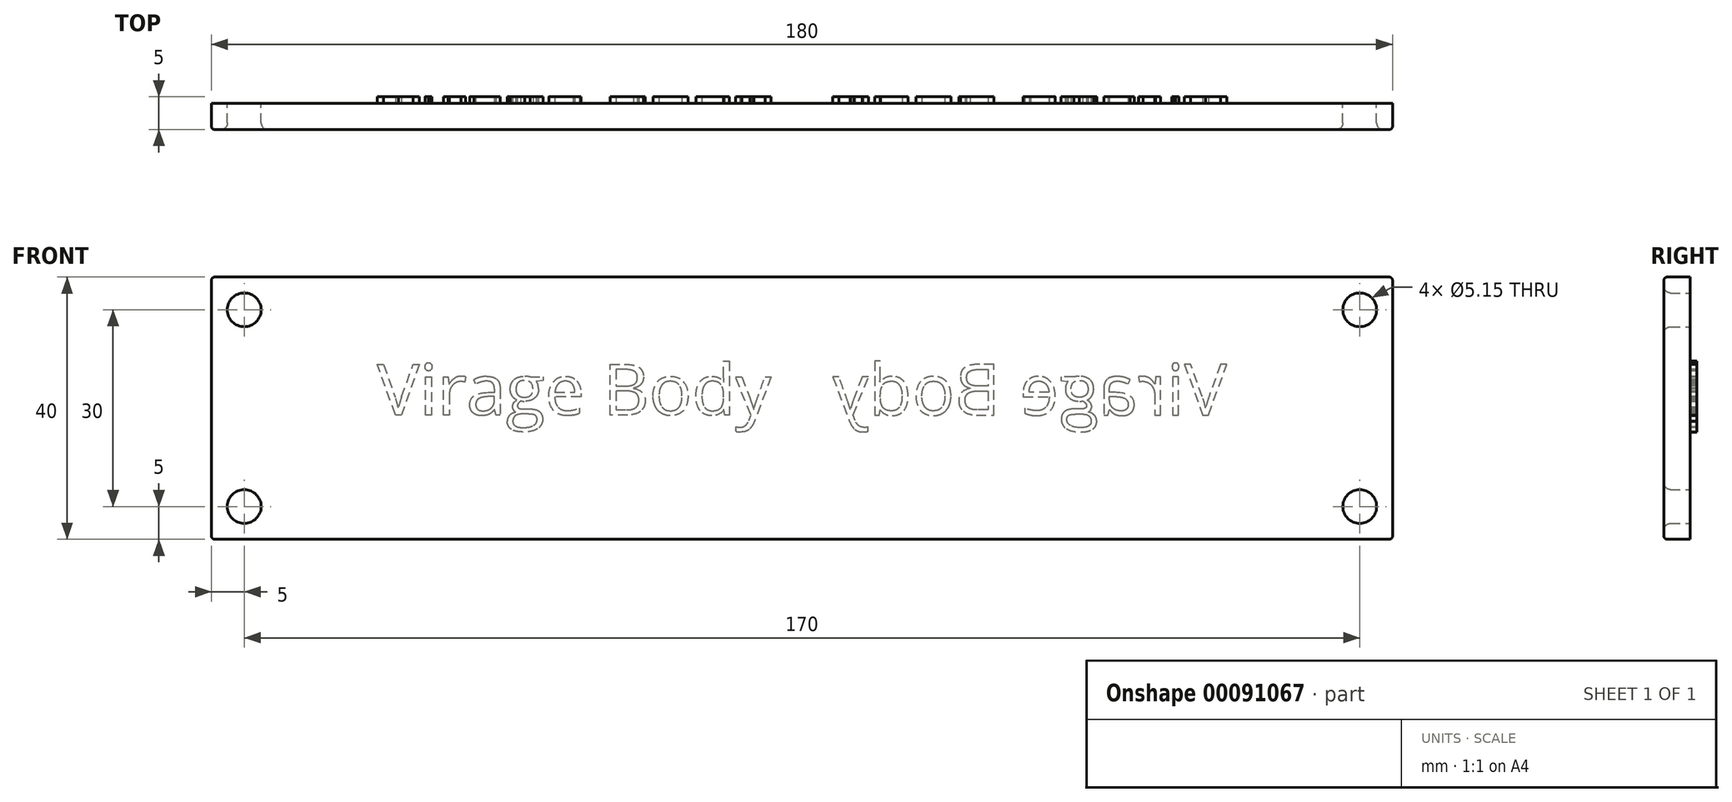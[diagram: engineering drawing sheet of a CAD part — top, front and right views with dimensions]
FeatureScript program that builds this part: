
annotation { "Feature Type Name" : "Feature", "Feature Type Description" : "" }
export const myFeature = defineFeature(function(context is Context, id is Id, definition is map)
    precondition{}
    {
        {
            var Q0;
            Q0=qCreatedBy(makeId("Front.planeOp"),FACE);
            var sketch = newSketch(context, id + "F0", { "sketchPlane" : qUnion([Q0])});
            skLineSegment(sketch, "E0.bottom", {"start": v(-90, -20) * mm, "end": v(90, -20) * mm});
            skLineSegment(sketch, "E0.top", {"start": v(-90, 20) * mm, "end": v(90, 20) * mm});
            skLineSegment(sketch, "E0.left", {"start": v(-90, -20) * mm, "end": v(-90, 20) * mm});
            skLineSegment(sketch, "E0.right", {"start": v(90, -20) * mm, "end": v(90, 20) * mm});
            skPoint(sketch, "E0.middle", {"position": v(0, 0) * mm});
            skCircle(sketch, "E1", {"center": v(-85, 15) * mm, "radius": 2.58 * mm});
            skPoint(sketch, "E2.start.orphan", {"position": v(-90, 0) * mm});
            skPoint(sketch, "E3.orphan", {"position": v(0, 20) * mm});
            skPoint(sketch, "E4.end.orphan", {"position": v(0, -20) * mm});
            skLineSegment(sketch, "E5", {"start": v(-90, 0) * mm, "end": v(0, 0) * mm, "construction": true});
            skLineSegment(sketch, "E6", {"start": v(0, 20) * mm, "end": v(0, -20) * mm, "construction": true});
            skCircle(sketch, "E7.MirrorC", {"center": v(-85, -15) * mm, "radius": 2.58 * mm});
            skCircle(sketch, "E8.MirrorC", {"center": v(85, 15) * mm, "radius": 2.58 * mm});
            skCircle(sketch, "E9.MirrorC", {"center": v(85, -15) * mm, "radius": 2.58 * mm});
            skSolve(sketch);
        }
        {
            var Q0;
            Q0=makeQuery(id+"F0.imprint","IMPRINT",FACE,{"disambiguationData":[TD([[makeQuery(id+"F0.imprint","IMPRINT",EDGE,{"derivedFrom":sQuery(id+"F0.wireOp",EDGE,"E0.bottom")}),1.0]])]});
            extrude(context, id + "F1", {"entities" : qUnion([Q0]), "depth" : 4 * mm});
        }
        {
            var Q0;
            Q0=makeQuery(id+"F1.opExtrude","CAP_EDGE",EDGE,{"disambiguationData":[OSD([sQuery(id+"F0.wireOp",EDGE,"E1")])],"isStart":false});
            var Q1;
            Q1=makeQuery(id+"F1.opExtrude","CAP_EDGE",EDGE,{"disambiguationData":[OSD([sQuery(id+"F0.wireOp",EDGE,"f5b72a5b-8583-449a-bdbf-9ac5a681e1fd0.MirrorC")])],"isStart":false});
            var Q2;
            Q2=makeQuery(id+"F1.opExtrude","CAP_EDGE",EDGE,{"disambiguationData":[OSD([sQuery(id+"F0.wireOp",EDGE,"2623e306-60f4-4522-aa65-1e3e8c2cf5b60.MirrorC")])],"isStart":false});
            var Q3;
            Q3=makeQuery(id+"F1.opExtrude","CAP_EDGE",EDGE,{"disambiguationData":[OSD([sQuery(id+"F0.wireOp",EDGE,"be81a34d-1d50-4ce7-a7a8-4484a1701fac0.MirrorC")])],"isStart":false});
            var Q4;
            Q4=makeQuery(id+"F1.opExtrude","CAP_EDGE",EDGE,{"disambiguationData":[OSD([sQuery(id+"F0.wireOp",EDGE,"E7.MirrorC")])],"isStart":false});
            var Q5;
            Q5=makeQuery(id+"F1.opExtrude","CAP_EDGE",EDGE,{"disambiguationData":[OSD([sQuery(id+"F0.wireOp",EDGE,"E8.MirrorC")])],"isStart":false});
            var Q6;
            Q6=makeQuery(id+"F1.opExtrude","CAP_EDGE",EDGE,{"disambiguationData":[OSD([sQuery(id+"F0.wireOp",EDGE,"E9.MirrorC")])],"isStart":false});
            fillet(context, id + "F2", {"entities" : qUnion([Q0, Q1, Q2, Q3, Q4, Q5, Q6]), "radius" : 1 * mm, "tangentPropagation" : true, "allowEdgeOverflow" : false});
        }
        {
            var Q0;
            Q0=makeQuery(id+"F1.opExtrude","CAP_EDGE",EDGE,{"disambiguationData":[OSD([sQuery(id+"F0.wireOp",EDGE,"E0.top")])],"isStart":false});
            var Q1;
            Q1=makeQuery(id+"F1.opExtrude","CAP_EDGE",EDGE,{"disambiguationData":[OSD([sQuery(id+"F0.wireOp",EDGE,"E0.left")])],"isStart":false});
            var Q2;
            Q2=makeQuery(id+"F1.opExtrude","CAP_EDGE",EDGE,{"disambiguationData":[OSD([sQuery(id+"F0.wireOp",EDGE,"E0.bottom")])],"isStart":false});
            var Q3;
            Q3=makeQuery(id+"F1.opExtrude","CAP_EDGE",EDGE,{"disambiguationData":[OSD([sQuery(id+"F0.wireOp",EDGE,"E0.right")])],"isStart":false});
            var Q4;
            Q4=makeQuery(id+"F1.opExtrude","SWEPT_EDGE",EDGE,{"disambiguationData":[OSD([sQuery(id+"F0.wireOp",EDGE,"E0.top"),sQuery(id+"F0.wireOp",EDGE,"E0.left")])]});
            var Q5;
            Q5=makeQuery(id+"F1.opExtrude","SWEPT_EDGE",EDGE,{"disambiguationData":[OSD([sQuery(id+"F0.wireOp",EDGE,"E0.bottom"),sQuery(id+"F0.wireOp",EDGE,"E0.left")])]});
            var Q6;
            Q6=makeQuery(id+"F1.opExtrude","SWEPT_EDGE",EDGE,{"disambiguationData":[OSD([sQuery(id+"F0.wireOp",EDGE,"E0.top"),sQuery(id+"F0.wireOp",EDGE,"E0.right")])]});
            var Q7;
            Q7=makeQuery(id+"F1.opExtrude","SWEPT_EDGE",EDGE,{"disambiguationData":[OSD([sQuery(id+"F0.wireOp",EDGE,"E0.bottom"),sQuery(id+"F0.wireOp",EDGE,"E0.right")])]});
            fillet(context, id + "F3", {"entities" : qUnion([Q0, Q1, Q2, Q3, Q4, Q5, Q6, Q7]), "radius" : .5 * mm, "tangentPropagation" : true, "allowEdgeOverflow" : false});
        }
        {
            var Q0;
            Q0=makeQuery(id+"F1.opExtrude","CAP_FACE",FACE,{"disambiguationData":[OSD([sQuery(id+"F0.wireOp",EDGE,"E0.bottom"),sQuery(id+"F0.wireOp",EDGE,"E0.top"),sQuery(id+"F0.wireOp",EDGE,"E0.left"),sQuery(id+"F0.wireOp",EDGE,"E0.right"),sQuery(id+"F0.wireOp",EDGE,"E1"),sQuery(id+"F0.wireOp",EDGE,"E7.MirrorC"),sQuery(id+"F0.wireOp",EDGE,"E8.MirrorC"),sQuery(id+"F0.wireOp",EDGE,"E9.MirrorC")])],"isStart":true});
            var sketch = newSketch(context, id + "F4", { "sketchPlane" : qUnion([Q0])});
            skText(sketch, "E10", { "text": "Virage Body", "fontName": "OpenSans-Regular.ttf"});
            skLineSegment(sketch, "E11", {"start": v(0, 20) * mm, "end": v(0, -20) * mm, "construction": true});
            const initialGuessF4  = {"E10": [-0.06473, -0.00103, 1, 0, 0.00779]};
            skSetInitialGuess(sketch, initialGuessF4);
            skSolve(sketch);
        }
        {
            var Q0;
            Q0=qSketchRegion(id+"F4",true);
            extrude(context, id + "F5", {"entities" : qUnion([Q0]), "operationType" : NewBodyOperationType.ADD, "depth" : 1 * mm});
        }
        {
            var Q0;
            Q0=makeQuery(id+"F1.opExtrude","SWEPT_BODY",BODY,{"disambiguationData":[OSD([sQuery(id+"F0.wireOp",EDGE,"E0.bottom"),sQuery(id+"F0.wireOp",EDGE,"E0.top"),sQuery(id+"F0.wireOp",EDGE,"E0.left"),sQuery(id+"F0.wireOp",EDGE,"E0.right"),sQuery(id+"F0.wireOp",EDGE,"E1"),sQuery(id+"F0.wireOp",EDGE,"E7.MirrorC"),sQuery(id+"F0.wireOp",EDGE,"E8.MirrorC"),sQuery(id+"F0.wireOp",EDGE,"E9.MirrorC")])]});
            var Q1;
            Q1=makeQuery(id+"F5.opExtrude","SWEPT_FACE",FACE,{"disambiguationData":[OSD([sQuery(id+"F4.wireOp",EDGE,"E10.sketch_text.stroke-94")])]});
            var Q2;
            Q2=makeQuery(id+"F5.opExtrude","SWEPT_FACE",FACE,{"disambiguationData":[OSD([sQuery(id+"F4.wireOp",EDGE,"E10.sketch_text.stroke-169")])]});
            var Q3;
            Q3=makeQuery(id+"F5.opExtrude","SWEPT_FACE",FACE,{"disambiguationData":[OSD([sQuery(id+"F4.wireOp",EDGE,"E10.sketch_text.stroke-185")])]});
            var Q4;
            Q4=makeQuery(id+"F5.opExtrude","SWEPT_FACE",FACE,{"disambiguationData":[OSD([sQuery(id+"F4.wireOp",EDGE,"E10.sketch_text.stroke-125")])]});
            var Q5;
            Q5=makeQuery(id+"F5.opExtrude","SWEPT_FACE",FACE,{"disambiguationData":[OSD([sQuery(id+"F4.wireOp",EDGE,"E10.sketch_text.stroke-155")])]});
            var Q6;
            Q6=makeQuery(id+"F5.opExtrude","SWEPT_FACE",FACE,{"disambiguationData":[OSD([sQuery(id+"F4.wireOp",EDGE,"E10.sketch_text.stroke-65")])]});
            var Q7;
            Q7=makeQuery(id+"F5.opExtrude","SWEPT_FACE",FACE,{"disambiguationData":[OSD([sQuery(id+"F4.wireOp",EDGE,"E10.sketch_text.stroke-81")])]});
            var Q8;
            Q8=makeQuery(id+"F5.opExtrude","SWEPT_FACE",FACE,{"disambiguationData":[OSD([sQuery(id+"F4.wireOp",EDGE,"E10.sketch_text.stroke-67")])]});
            var Q9;
            Q9=makeQuery(id+"F5.opExtrude","SWEPT_FACE",FACE,{"disambiguationData":[OSD([sQuery(id+"F4.wireOp",EDGE,"E10.sketch_text.stroke-99")])]});
            var Q10;
            Q10=makeQuery(id+"F5.opExtrude","SWEPT_FACE",FACE,{"disambiguationData":[OSD([sQuery(id+"F4.wireOp",EDGE,"E10.sketch_text.stroke-127")])]});
            var Q11;
            Q11=makeQuery(id+"F5.opExtrude","SWEPT_FACE",FACE,{"disambiguationData":[OSD([sQuery(id+"F4.wireOp",EDGE,"E10.sketch_text.stroke-10")])]});
            var Q12;
            Q12=makeQuery(id+"F5.opExtrude","CAP_FACE",FACE,{"disambiguationData":[OSD([sQuery(id+"F4.wireOp",EDGE,"E10.sketch_text.stroke-9"),sQuery(id+"F4.wireOp",EDGE,"E10.sketch_text.stroke-10"),sQuery(id+"F4.wireOp",EDGE,"E10.sketch_text.stroke-11"),sQuery(id+"F4.wireOp",EDGE,"E10.sketch_text.stroke-12")])],"isStart":false});
            var Q13;
            Q13=makeQuery(id+"F5.opExtrude","SWEPT_FACE",FACE,{"disambiguationData":[OSD([sQuery(id+"F4.wireOp",EDGE,"E10.sketch_text.stroke-154")])]});
            var Q14;
            Q14=makeQuery(id+"F5.opExtrude","SWEPT_FACE",FACE,{"disambiguationData":[OSD([sQuery(id+"F4.wireOp",EDGE,"E10.sketch_text.stroke-1")])]});
            var Q15;
            Q15=makeQuery(id+"F5.opExtrude","CAP_FACE",FACE,{"disambiguationData":[OSD([sQuery(id+"F4.wireOp",EDGE,"E10.sketch_text.stroke-124"),sQuery(id+"F4.wireOp",EDGE,"E10.sketch_text.stroke-125"),sQuery(id+"F4.wireOp",EDGE,"E10.sketch_text.stroke-126"),sQuery(id+"F4.wireOp",EDGE,"E10.sketch_text.stroke-127"),sQuery(id+"F4.wireOp",EDGE,"E10.sketch_text.stroke-128"),sQuery(id+"F4.wireOp",EDGE,"E10.sketch_text.stroke-129"),sQuery(id+"F4.wireOp",EDGE,"E10.sketch_text.stroke-130"),sQuery(id+"F4.wireOp",EDGE,"E10.sketch_text.stroke-131"),sQuery(id+"F4.wireOp",EDGE,"E10.sketch_text.stroke-132"),sQuery(id+"F4.wireOp",EDGE,"E10.sketch_text.stroke-133"),sQuery(id+"F4.wireOp",EDGE,"E10.sketch_text.stroke-134"),sQuery(id+"F4.wireOp",EDGE,"E10.sketch_text.stroke-135"),sQuery(id+"F4.wireOp",EDGE,"E10.sketch_text.stroke-136"),sQuery(id+"F4.wireOp",EDGE,"E10.sketch_text.stroke-137"),sQuery(id+"F4.wireOp",EDGE,"E10.sketch_text.stroke-138")])],"isStart":false});
            var Q16;
            Q16=makeQuery(id+"F5.opExtrude","CAP_FACE",FACE,{"disambiguationData":[OSD([sQuery(id+"F4.wireOp",EDGE,"E10.sketch_text.stroke-34"),sQuery(id+"F4.wireOp",EDGE,"E10.sketch_text.stroke-35"),sQuery(id+"F4.wireOp",EDGE,"E10.sketch_text.stroke-36"),sQuery(id+"F4.wireOp",EDGE,"E10.sketch_text.stroke-37"),sQuery(id+"F4.wireOp",EDGE,"E10.sketch_text.stroke-38"),sQuery(id+"F4.wireOp",EDGE,"E10.sketch_text.stroke-39"),sQuery(id+"F4.wireOp",EDGE,"E10.sketch_text.stroke-40"),sQuery(id+"F4.wireOp",EDGE,"E10.sketch_text.stroke-41"),sQuery(id+"F4.wireOp",EDGE,"E10.sketch_text.stroke-42"),sQuery(id+"F4.wireOp",EDGE,"E10.sketch_text.stroke-43"),sQuery(id+"F4.wireOp",EDGE,"E10.sketch_text.stroke-44"),sQuery(id+"F4.wireOp",EDGE,"E10.sketch_text.stroke-45"),sQuery(id+"F4.wireOp",EDGE,"E10.sketch_text.stroke-46"),sQuery(id+"F4.wireOp",EDGE,"E10.sketch_text.stroke-47"),sQuery(id+"F4.wireOp",EDGE,"E10.sketch_text.stroke-48"),sQuery(id+"F4.wireOp",EDGE,"E10.sketch_text.stroke-49"),sQuery(id+"F4.wireOp",EDGE,"E10.sketch_text.stroke-50"),sQuery(id+"F4.wireOp",EDGE,"E10.sketch_text.stroke-51"),sQuery(id+"F4.wireOp",EDGE,"E10.sketch_text.stroke-52"),sQuery(id+"F4.wireOp",EDGE,"E10.sketch_text.stroke-53"),sQuery(id+"F4.wireOp",EDGE,"E10.sketch_text.stroke-54"),sQuery(id+"F4.wireOp",EDGE,"E10.sketch_text.stroke-55"),sQuery(id+"F4.wireOp",EDGE,"E10.sketch_text.stroke-56"),sQuery(id+"F4.wireOp",EDGE,"E10.sketch_text.stroke-57"),sQuery(id+"F4.wireOp",EDGE,"E10.sketch_text.stroke-58"),sQuery(id+"F4.wireOp",EDGE,"E10.sketch_text.stroke-59"),sQuery(id+"F4.wireOp",EDGE,"E10.sketch_text.stroke-60")])],"isStart":false});
            var Q17;
            Q17=makeQuery(id+"F5.opExtrude","SWEPT_FACE",FACE,{"disambiguationData":[OSD([sQuery(id+"F4.wireOp",EDGE,"E10.sketch_text.stroke-50")])]});
            var Q18;
            Q18=makeQuery(id+"F5.opExtrude","SWEPT_FACE",FACE,{"disambiguationData":[OSD([sQuery(id+"F4.wireOp",EDGE,"E10.sketch_text.stroke-2")])]});
            var Q19;
            Q19=makeQuery(id+"F5.opExtrude","SWEPT_FACE",FACE,{"disambiguationData":[OSD([sQuery(id+"F4.wireOp",EDGE,"E10.sketch_text.stroke-3")])]});
            var Q20;
            Q20=makeQuery(id+"F5.opExtrude","SWEPT_FACE",FACE,{"disambiguationData":[OSD([sQuery(id+"F4.wireOp",EDGE,"E10.sketch_text.stroke-5")])]});
            var Q21;
            Q21=makeQuery(id+"F5.opExtrude","SWEPT_FACE",FACE,{"disambiguationData":[OSD([sQuery(id+"F4.wireOp",EDGE,"E10.sketch_text.stroke-8")])]});
            var Q22;
            Q22=makeQuery(id+"F5.opExtrude","SWEPT_FACE",FACE,{"disambiguationData":[OSD([sQuery(id+"F4.wireOp",EDGE,"E10.sketch_text.stroke-98")])]});
            var Q23;
            Q23=makeQuery(id+"F5.opExtrude","SWEPT_FACE",FACE,{"disambiguationData":[OSD([sQuery(id+"F4.wireOp",EDGE,"E10.sketch_text.stroke-66")])]});
            var Q24;
            Q24=makeQuery(id+"F5.opExtrude","SWEPT_FACE",FACE,{"disambiguationData":[OSD([sQuery(id+"F4.wireOp",EDGE,"E10.sketch_text.stroke-153")])]});
            var Q25;
            Q25=makeQuery(id+"F5.opExtrude","SWEPT_FACE",FACE,{"disambiguationData":[OSD([sQuery(id+"F4.wireOp",EDGE,"E10.sketch_text.stroke-126")])]});
            var Q26;
            Q26=makeQuery(id+"F5.opExtrude","SWEPT_FACE",FACE,{"disambiguationData":[OSD([sQuery(id+"F4.wireOp",EDGE,"E10.sketch_text.stroke-183")])]});
            var Q27;
            Q27=makeQuery(id+"F5.opExtrude","SWEPT_FACE",FACE,{"disambiguationData":[OSD([sQuery(id+"F4.wireOp",EDGE,"E10.sketch_text.stroke-109")])]});
            var Q28;
            Q28=makeQuery(id+"F5.opExtrude","SWEPT_FACE",FACE,{"disambiguationData":[OSD([sQuery(id+"F4.wireOp",EDGE,"E10.sketch_text.stroke-186")])]});
            var Q29;
            Q29=makeQuery(id+"F5.opExtrude","SWEPT_FACE",FACE,{"disambiguationData":[OSD([sQuery(id+"F4.wireOp",EDGE,"E10.sketch_text.stroke-79")])]});
            var Q30;
            Q30=makeQuery(id+"F5.opExtrude","SWEPT_FACE",FACE,{"disambiguationData":[OSD([sQuery(id+"F4.wireOp",EDGE,"E10.sketch_text.stroke-110")])]});
            var Q31;
            Q31=makeQuery(id+"F5.opExtrude","SWEPT_FACE",FACE,{"disambiguationData":[OSD([sQuery(id+"F4.wireOp",EDGE,"E10.sketch_text.stroke-38")])]});
            var Q32;
            Q32=makeQuery(id+"F5.opExtrude","SWEPT_FACE",FACE,{"disambiguationData":[OSD([sQuery(id+"F4.wireOp",EDGE,"E10.sketch_text.stroke-24")])]});
            var Q33;
            Q33=makeQuery(id+"F5.opExtrude","SWEPT_FACE",FACE,{"disambiguationData":[OSD([sQuery(id+"F4.wireOp",EDGE,"E10.sketch_text.stroke-12")])]});
            var Q34;
            Q34=makeQuery(id+"F5.opExtrude","SWEPT_FACE",FACE,{"disambiguationData":[OSD([sQuery(id+"F4.wireOp",EDGE,"E10.sketch_text.stroke-100")])]});
            var Q35;
            Q35=makeQuery(id+"F5.opExtrude","SWEPT_FACE",FACE,{"disambiguationData":[OSD([sQuery(id+"F4.wireOp",EDGE,"E10.sketch_text.stroke-158")])]});
            var Q36;
            Q36=makeQuery(id+"F5.opExtrude","SWEPT_FACE",FACE,{"disambiguationData":[OSD([sQuery(id+"F4.wireOp",EDGE,"E10.sketch_text.stroke-142")])]});
            var Q37;
            Q37=makeQuery(id+"F5.opExtrude","SWEPT_FACE",FACE,{"disambiguationData":[OSD([sQuery(id+"F4.wireOp",EDGE,"E10.sketch_text.stroke-54")])]});
            var Q38;
            Q38=makeQuery(id+"F5.opExtrude","SWEPT_FACE",FACE,{"disambiguationData":[OSD([sQuery(id+"F4.wireOp",EDGE,"E10.sketch_text.stroke-25")])]});
            var Q39;
            Q39=makeQuery(id+"F5.opExtrude","SWEPT_FACE",FACE,{"disambiguationData":[OSD([sQuery(id+"F4.wireOp",EDGE,"E10.sketch_text.stroke-101")])]});
            var Q40;
            Q40=makeQuery(id+"F5.opExtrude","SWEPT_FACE",FACE,{"disambiguationData":[OSD([sQuery(id+"F4.wireOp",EDGE,"E10.sketch_text.stroke-69")])]});
            var Q41;
            Q41=makeQuery(id+"F5.opExtrude","SWEPT_FACE",FACE,{"disambiguationData":[OSD([sQuery(id+"F4.wireOp",EDGE,"E10.sketch_text.stroke-159")])]});
            var Q42;
            Q42=makeQuery(id+"F5.opExtrude","SWEPT_FACE",FACE,{"disambiguationData":[OSD([sQuery(id+"F4.wireOp",EDGE,"E10.sketch_text.stroke-85")])]});
            var Q43;
            Q43=makeQuery(id+"F5.opExtrude","SWEPT_FACE",FACE,{"disambiguationData":[OSD([sQuery(id+"F4.wireOp",EDGE,"E10.sketch_text.stroke-173")])]});
            var Q44;
            Q44=makeQuery(id+"F5.opExtrude","SWEPT_FACE",FACE,{"disambiguationData":[OSD([sQuery(id+"F4.wireOp",EDGE,"E10.sketch_text.stroke-40")])]});
            var Q45;
            Q45=makeQuery(id+"F5.opExtrude","SWEPT_FACE",FACE,{"disambiguationData":[OSD([sQuery(id+"F4.wireOp",EDGE,"E10.sketch_text.stroke-102")])]});
            var Q46;
            Q46=makeQuery(id+"F5.opExtrude","SWEPT_FACE",FACE,{"disambiguationData":[OSD([sQuery(id+"F4.wireOp",EDGE,"E10.sketch_text.stroke-86")])]});
            var Q47;
            Q47=makeQuery(id+"F5.opExtrude","SWEPT_FACE",FACE,{"disambiguationData":[OSD([sQuery(id+"F4.wireOp",EDGE,"E10.sketch_text.stroke-130")])]});
            var Q48;
            Q48=makeQuery(id+"F5.opExtrude","SWEPT_FACE",FACE,{"disambiguationData":[OSD([sQuery(id+"F4.wireOp",EDGE,"E10.sketch_text.stroke-103")])]});
            var Q49;
            Q49=makeQuery(id+"F5.opExtrude","SWEPT_FACE",FACE,{"disambiguationData":[OSD([sQuery(id+"F4.wireOp",EDGE,"E10.sketch_text.stroke-87")])]});
            var Q50;
            Q50=makeQuery(id+"F5.opExtrude","SWEPT_FACE",FACE,{"disambiguationData":[OSD([sQuery(id+"F4.wireOp",EDGE,"E10.sketch_text.stroke-145")])]});
            var Q51;
            Q51=makeQuery(id+"F5.opExtrude","SWEPT_FACE",FACE,{"disambiguationData":[OSD([sQuery(id+"F4.wireOp",EDGE,"E10.sketch_text.stroke-131")])]});
            var Q52;
            Q52=makeQuery(id+"F5.opExtrude","SWEPT_FACE",FACE,{"disambiguationData":[OSD([sQuery(id+"F4.wireOp",EDGE,"E10.sketch_text.stroke-28")])]});
            var Q53;
            Q53=makeQuery(id+"F5.opExtrude","SWEPT_FACE",FACE,{"disambiguationData":[OSD([sQuery(id+"F4.wireOp",EDGE,"E10.sketch_text.stroke-14")])]});
            var Q54;
            Q54=makeQuery(id+"F5.opExtrude","SWEPT_FACE",FACE,{"disambiguationData":[OSD([sQuery(id+"F4.wireOp",EDGE,"E10.sketch_text.stroke-88")])]});
            var Q55;
            Q55=makeQuery(id+"F5.opExtrude","SWEPT_FACE",FACE,{"disambiguationData":[OSD([sQuery(id+"F4.wireOp",EDGE,"E10.sketch_text.stroke-162")])]});
            var Q56;
            Q56=makeQuery(id+"F5.opExtrude","SWEPT_FACE",FACE,{"disambiguationData":[OSD([sQuery(id+"F4.wireOp",EDGE,"E10.sketch_text.stroke-176")])]});
            var Q57;
            Q57=makeQuery(id+"F5.opExtrude","SWEPT_FACE",FACE,{"disambiguationData":[OSD([sQuery(id+"F4.wireOp",EDGE,"E10.sketch_text.stroke-73")])]});
            var Q58;
            Q58=makeQuery(id+"F5.opExtrude","SWEPT_FACE",FACE,{"disambiguationData":[OSD([sQuery(id+"F4.wireOp",EDGE,"E10.sketch_text.stroke-59")])]});
            var Q59;
            Q59=makeQuery(id+"F5.opExtrude","SWEPT_FACE",FACE,{"disambiguationData":[OSD([sQuery(id+"F4.wireOp",EDGE,"E10.sketch_text.stroke-133")])]});
            var Q60;
            Q60=makeQuery(id+"F5.opExtrude","SWEPT_FACE",FACE,{"disambiguationData":[OSD([sQuery(id+"F4.wireOp",EDGE,"E10.sketch_text.stroke-119")])]});
            var Q61;
            Q61=makeQuery(id+"F5.opExtrude","SWEPT_FACE",FACE,{"disambiguationData":[OSD([sQuery(id+"F4.wireOp",EDGE,"E10.sketch_text.stroke-74")])]});
            var Q62;
            Q62=makeQuery(id+"F5.opExtrude","SWEPT_FACE",FACE,{"disambiguationData":[OSD([sQuery(id+"F4.wireOp",EDGE,"E10.sketch_text.stroke-44")])]});
            var Q63;
            Q63=makeQuery(id+"F5.opExtrude","SWEPT_FACE",FACE,{"disambiguationData":[OSD([sQuery(id+"F4.wireOp",EDGE,"E10.sketch_text.stroke-120")])]});
            var Q64;
            Q64=makeQuery(id+"F5.opExtrude","SWEPT_FACE",FACE,{"disambiguationData":[OSD([sQuery(id+"F4.wireOp",EDGE,"E10.sketch_text.stroke-90")])]});
            var Q65;
            Q65=makeQuery(id+"F5.opExtrude","SWEPT_FACE",FACE,{"disambiguationData":[OSD([sQuery(id+"F4.wireOp",EDGE,"E10.sketch_text.stroke-178")])]});
            var Q66;
            Q66=makeQuery(id+"F5.opExtrude","SWEPT_FACE",FACE,{"disambiguationData":[OSD([sQuery(id+"F4.wireOp",EDGE,"E10.sketch_text.stroke-45")])]});
            var Q67;
            Q67=makeQuery(id+"F5.opExtrude","SWEPT_FACE",FACE,{"disambiguationData":[OSD([sQuery(id+"F4.wireOp",EDGE,"E10.sketch_text.stroke-31")])]});
            var Q68;
            Q68=makeQuery(id+"F5.opExtrude","SWEPT_FACE",FACE,{"disambiguationData":[OSD([sQuery(id+"F4.wireOp",EDGE,"E10.sketch_text.stroke-135")])]});
            var Q69;
            Q69=makeQuery(id+"F5.opExtrude","SWEPT_FACE",FACE,{"disambiguationData":[OSD([sQuery(id+"F4.wireOp",EDGE,"E10.sketch_text.stroke-179")])]});
            var Q70;
            Q70=makeQuery(id+"F5.opExtrude","SWEPT_FACE",FACE,{"disambiguationData":[OSD([sQuery(id+"F4.wireOp",EDGE,"E10.sketch_text.stroke-165")])]});
            var Q71;
            Q71=makeQuery(id+"F5.opExtrude","SWEPT_FACE",FACE,{"disambiguationData":[OSD([sQuery(id+"F4.wireOp",EDGE,"E10.sketch_text.stroke-149")])]});
            var Q72;
            Q72=makeQuery(id+"F5.opExtrude","SWEPT_FACE",FACE,{"disambiguationData":[OSD([sQuery(id+"F4.wireOp",EDGE,"E10.sketch_text.stroke-136")])]});
            var Q73;
            Q73=makeQuery(id+"F5.opExtrude","SWEPT_FACE",FACE,{"disambiguationData":[OSD([sQuery(id+"F4.wireOp",EDGE,"E10.sketch_text.stroke-122")])]});
            var Q74;
            Q74=makeQuery(id+"F5.opExtrude","SWEPT_FACE",FACE,{"disambiguationData":[OSD([sQuery(id+"F4.wireOp",EDGE,"E10.sketch_text.stroke-106")])]});
            var Q75;
            Q75=makeQuery(id+"F5.opExtrude","SWEPT_FACE",FACE,{"disambiguationData":[OSD([sQuery(id+"F4.wireOp",EDGE,"E10.sketch_text.stroke-180")])]});
            var Q76;
            Q76=makeQuery(id+"F5.opExtrude","SWEPT_FACE",FACE,{"disambiguationData":[OSD([sQuery(id+"F4.wireOp",EDGE,"E10.sketch_text.stroke-166")])]});
            var Q77;
            Q77=makeQuery(id+"F5.opExtrude","SWEPT_FACE",FACE,{"disambiguationData":[OSD([sQuery(id+"F4.wireOp",EDGE,"E10.sketch_text.stroke-150")])]});
            var Q78;
            Q78=makeQuery(id+"F5.opExtrude","SWEPT_FACE",FACE,{"disambiguationData":[OSD([sQuery(id+"F4.wireOp",EDGE,"E10.sketch_text.stroke-76")])]});
            var Q79;
            Q79=makeQuery(id+"F5.opExtrude","SWEPT_FACE",FACE,{"disambiguationData":[OSD([sQuery(id+"F4.wireOp",EDGE,"E10.sketch_text.stroke-32")])]});
            var Q80;
            Q80=makeQuery(id+"F5.opExtrude","SWEPT_FACE",FACE,{"disambiguationData":[OSD([sQuery(id+"F4.wireOp",EDGE,"E10.sketch_text.stroke-181")])]});
            var Q81;
            Q81=makeQuery(id+"F5.opExtrude","SWEPT_FACE",FACE,{"disambiguationData":[OSD([sQuery(id+"F4.wireOp",EDGE,"E10.sketch_text.stroke-47")])]});
            var Q82;
            Q82=makeQuery(id+"F5.opExtrude","SWEPT_FACE",FACE,{"disambiguationData":[OSD([sQuery(id+"F4.wireOp",EDGE,"E10.sketch_text.stroke-123")])]});
            var Q83;
            Q83=makeQuery(id+"F5.opExtrude","SWEPT_FACE",FACE,{"disambiguationData":[OSD([sQuery(id+"F4.wireOp",EDGE,"E10.sketch_text.stroke-107")])]});
            var Q84;
            Q84=makeQuery(id+"F5.opExtrude","SWEPT_FACE",FACE,{"disambiguationData":[OSD([sQuery(id+"F4.wireOp",EDGE,"E10.sketch_text.stroke-48")])]});
            var Q85;
            Q85=makeQuery(id+"F5.opExtrude","SWEPT_FACE",FACE,{"disambiguationData":[OSD([sQuery(id+"F4.wireOp",EDGE,"E10.sketch_text.stroke-124")])]});
            var Q86;
            Q86=makeQuery(id+"F5.opExtrude","SWEPT_FACE",FACE,{"disambiguationData":[OSD([sQuery(id+"F4.wireOp",EDGE,"E10.sketch_text.stroke-108")])]});
            var Q87;
            Q87=makeQuery(id+"F5.opExtrude","CAP_FACE",FACE,{"disambiguationData":[OSD([sQuery(id+"F4.wireOp",EDGE,"E10.sketch_text.stroke-139"),sQuery(id+"F4.wireOp",EDGE,"E10.sketch_text.stroke-140"),sQuery(id+"F4.wireOp",EDGE,"E10.sketch_text.stroke-141"),sQuery(id+"F4.wireOp",EDGE,"E10.sketch_text.stroke-142"),sQuery(id+"F4.wireOp",EDGE,"E10.sketch_text.stroke-143"),sQuery(id+"F4.wireOp",EDGE,"E10.sketch_text.stroke-144"),sQuery(id+"F4.wireOp",EDGE,"E10.sketch_text.stroke-145"),sQuery(id+"F4.wireOp",EDGE,"E10.sketch_text.stroke-146"),sQuery(id+"F4.wireOp",EDGE,"E10.sketch_text.stroke-147"),sQuery(id+"F4.wireOp",EDGE,"E10.sketch_text.stroke-148"),sQuery(id+"F4.wireOp",EDGE,"E10.sketch_text.stroke-149"),sQuery(id+"F4.wireOp",EDGE,"E10.sketch_text.stroke-150"),sQuery(id+"F4.wireOp",EDGE,"E10.sketch_text.stroke-151"),sQuery(id+"F4.wireOp",EDGE,"E10.sketch_text.stroke-152"),sQuery(id+"F4.wireOp",EDGE,"E10.sketch_text.stroke-153"),sQuery(id+"F4.wireOp",EDGE,"E10.sketch_text.stroke-154"),sQuery(id+"F4.wireOp",EDGE,"E10.sketch_text.stroke-155"),sQuery(id+"F4.wireOp",EDGE,"E10.sketch_text.stroke-156"),sQuery(id+"F4.wireOp",EDGE,"E10.sketch_text.stroke-157"),sQuery(id+"F4.wireOp",EDGE,"E10.sketch_text.stroke-158"),sQuery(id+"F4.wireOp",EDGE,"E10.sketch_text.stroke-159"),sQuery(id+"F4.wireOp",EDGE,"E10.sketch_text.stroke-160"),sQuery(id+"F4.wireOp",EDGE,"E10.sketch_text.stroke-161"),sQuery(id+"F4.wireOp",EDGE,"E10.sketch_text.stroke-162"),sQuery(id+"F4.wireOp",EDGE,"E10.sketch_text.stroke-163"),sQuery(id+"F4.wireOp",EDGE,"E10.sketch_text.stroke-164"),sQuery(id+"F4.wireOp",EDGE,"E10.sketch_text.stroke-165")])],"isStart":false});
            var Q88;
            Q88=makeQuery(id+"F5.opExtrude","CAP_FACE",FACE,{"disambiguationData":[OSD([sQuery(id+"F4.wireOp",EDGE,"E10.sketch_text.stroke-21"),sQuery(id+"F4.wireOp",EDGE,"E10.sketch_text.stroke-22"),sQuery(id+"F4.wireOp",EDGE,"E10.sketch_text.stroke-23"),sQuery(id+"F4.wireOp",EDGE,"E10.sketch_text.stroke-24"),sQuery(id+"F4.wireOp",EDGE,"E10.sketch_text.stroke-25"),sQuery(id+"F4.wireOp",EDGE,"E10.sketch_text.stroke-26"),sQuery(id+"F4.wireOp",EDGE,"E10.sketch_text.stroke-27"),sQuery(id+"F4.wireOp",EDGE,"E10.sketch_text.stroke-28"),sQuery(id+"F4.wireOp",EDGE,"E10.sketch_text.stroke-29"),sQuery(id+"F4.wireOp",EDGE,"E10.sketch_text.stroke-30"),sQuery(id+"F4.wireOp",EDGE,"E10.sketch_text.stroke-31"),sQuery(id+"F4.wireOp",EDGE,"E10.sketch_text.stroke-32"),sQuery(id+"F4.wireOp",EDGE,"E10.sketch_text.stroke-33")])],"isStart":false});
            var Q89;
            Q89=makeQuery(id+"F5.opExtrude","SWEPT_FACE",FACE,{"disambiguationData":[OSD([sQuery(id+"F4.wireOp",EDGE,"E10.sketch_text.stroke-113")])]});
            var Q90;
            Q90=makeQuery(id+"F5.opExtrude","SWEPT_FACE",FACE,{"disambiguationData":[OSD([sQuery(id+"F4.wireOp",EDGE,"E10.sketch_text.stroke-37")])]});
            var Q91;
            Q91=makeQuery(id+"F5.opExtrude","SWEPT_FACE",FACE,{"disambiguationData":[OSD([sQuery(id+"F4.wireOp",EDGE,"E10.sketch_text.stroke-187")])]});
            var Q92;
            Q92=makeQuery(id+"F5.opExtrude","SWEPT_FACE",FACE,{"disambiguationData":[OSD([sQuery(id+"F4.wireOp",EDGE,"E10.sketch_text.stroke-0")])]});
            var Q93;
            Q93=makeQuery(id+"F5.opExtrude","SWEPT_FACE",FACE,{"disambiguationData":[OSD([sQuery(id+"F4.wireOp",EDGE,"E10.sketch_text.stroke-4")])]});
            var Q94;
            Q94=makeQuery(id+"F5.opExtrude","SWEPT_FACE",FACE,{"disambiguationData":[OSD([sQuery(id+"F4.wireOp",EDGE,"E10.sketch_text.stroke-82")])]});
            var Q95;
            Q95=makeQuery(id+"F5.opExtrude","SWEPT_FACE",FACE,{"disambiguationData":[OSD([sQuery(id+"F4.wireOp",EDGE,"E10.sketch_text.stroke-52")])]});
            var Q96;
            Q96=makeQuery(id+"F5.opExtrude","SWEPT_FACE",FACE,{"disambiguationData":[OSD([sQuery(id+"F4.wireOp",EDGE,"E10.sketch_text.stroke-49")])]});
            var Q97;
            Q97=makeQuery(id+"F5.opExtrude","SWEPT_FACE",FACE,{"disambiguationData":[OSD([sQuery(id+"F4.wireOp",EDGE,"E10.sketch_text.stroke-63")])]});
            var Q98;
            Q98=makeQuery(id+"F5.opExtrude","SWEPT_FACE",FACE,{"disambiguationData":[OSD([sQuery(id+"F4.wireOp",EDGE,"E10.sketch_text.stroke-21")])]});
            var Q99;
            Q99=makeQuery(id+"F5.opExtrude","SWEPT_FACE",FACE,{"disambiguationData":[OSD([sQuery(id+"F4.wireOp",EDGE,"E10.sketch_text.stroke-128")])]});
            var Q100;
            Q100=makeQuery(id+"F5.opExtrude","SWEPT_FACE",FACE,{"disambiguationData":[OSD([sQuery(id+"F4.wireOp",EDGE,"E10.sketch_text.stroke-55")])]});
            var Q101;
            Q101=makeQuery(id+"F5.opExtrude","SWEPT_FACE",FACE,{"disambiguationData":[OSD([sQuery(id+"F4.wireOp",EDGE,"E10.sketch_text.stroke-26")])]});
            var Q102;
            Q102=makeQuery(id+"F5.opExtrude","SWEPT_FACE",FACE,{"disambiguationData":[OSD([sQuery(id+"F4.wireOp",EDGE,"E10.sketch_text.stroke-174")])]});
            var Q103;
            Q103=makeQuery(id+"F5.opExtrude","SWEPT_FACE",FACE,{"disambiguationData":[OSD([sQuery(id+"F4.wireOp",EDGE,"E10.sketch_text.stroke-104")])]});
            var Q104;
            Q104=makeQuery(id+"F5.opExtrude","SWEPT_FACE",FACE,{"disambiguationData":[OSD([sQuery(id+"F4.wireOp",EDGE,"E10.sketch_text.stroke-72")])]});
            var Q105;
            Q105=makeQuery(id+"F5.opExtrude","SWEPT_FACE",FACE,{"disambiguationData":[OSD([sQuery(id+"F4.wireOp",EDGE,"E10.sketch_text.stroke-132")])]});
            var Q106;
            Q106=makeQuery(id+"F5.opExtrude","SWEPT_FACE",FACE,{"disambiguationData":[OSD([sQuery(id+"F4.wireOp",EDGE,"E10.sketch_text.stroke-43")])]});
            var Q107;
            Q107=makeQuery(id+"F5.opExtrude","SWEPT_FACE",FACE,{"disambiguationData":[OSD([sQuery(id+"F4.wireOp",EDGE,"E10.sketch_text.stroke-15")])]});
            var Q108;
            Q108=makeQuery(id+"F5.opExtrude","SWEPT_FACE",FACE,{"disambiguationData":[OSD([sQuery(id+"F4.wireOp",EDGE,"E10.sketch_text.stroke-89")])]});
            var Q109;
            Q109=makeQuery(id+"F5.opExtrude","SWEPT_FACE",FACE,{"disambiguationData":[OSD([sQuery(id+"F4.wireOp",EDGE,"E10.sketch_text.stroke-163")])]});
            var Q110;
            Q110=makeQuery(id+"F5.opExtrude","SWEPT_FACE",FACE,{"disambiguationData":[OSD([sQuery(id+"F4.wireOp",EDGE,"E10.sketch_text.stroke-30")])]});
            var Q111;
            Q111=makeQuery(id+"F5.opExtrude","SWEPT_FACE",FACE,{"disambiguationData":[OSD([sQuery(id+"F4.wireOp",EDGE,"E10.sketch_text.stroke-134")])]});
            var Q112;
            Q112=makeQuery(id+"F5.opExtrude","SWEPT_FACE",FACE,{"disambiguationData":[OSD([sQuery(id+"F4.wireOp",EDGE,"E10.sketch_text.stroke-121")])]});
            var Q113;
            Q113=makeQuery(id+"F5.opExtrude","CAP_FACE",FACE,{"disambiguationData":[OSD([sQuery(id+"F4.wireOp",EDGE,"E10.sketch_text.stroke-105"),sQuery(id+"F4.wireOp",EDGE,"E10.sketch_text.stroke-106"),sQuery(id+"F4.wireOp",EDGE,"E10.sketch_text.stroke-107"),sQuery(id+"F4.wireOp",EDGE,"E10.sketch_text.stroke-108"),sQuery(id+"F4.wireOp",EDGE,"E10.sketch_text.stroke-109"),sQuery(id+"F4.wireOp",EDGE,"E10.sketch_text.stroke-110"),sQuery(id+"F4.wireOp",EDGE,"E10.sketch_text.stroke-111"),sQuery(id+"F4.wireOp",EDGE,"E10.sketch_text.stroke-112"),sQuery(id+"F4.wireOp",EDGE,"E10.sketch_text.stroke-113"),sQuery(id+"F4.wireOp",EDGE,"E10.sketch_text.stroke-114"),sQuery(id+"F4.wireOp",EDGE,"E10.sketch_text.stroke-115"),sQuery(id+"F4.wireOp",EDGE,"E10.sketch_text.stroke-116"),sQuery(id+"F4.wireOp",EDGE,"E10.sketch_text.stroke-117"),sQuery(id+"F4.wireOp",EDGE,"E10.sketch_text.stroke-118"),sQuery(id+"F4.wireOp",EDGE,"E10.sketch_text.stroke-119"),sQuery(id+"F4.wireOp",EDGE,"E10.sketch_text.stroke-120"),sQuery(id+"F4.wireOp",EDGE,"E10.sketch_text.stroke-121"),sQuery(id+"F4.wireOp",EDGE,"E10.sketch_text.stroke-122"),sQuery(id+"F4.wireOp",EDGE,"E10.sketch_text.stroke-123")])],"isStart":false});
            var Q114;
            Q114=makeQuery(id+"F5.opExtrude","SWEPT_FACE",FACE,{"disambiguationData":[OSD([sQuery(id+"F4.wireOp",EDGE,"E10.sketch_text.stroke-92")])]});
            var Q115;
            Q115=makeQuery(id+"F5.opExtrude","SWEPT_FACE",FACE,{"disambiguationData":[OSD([sQuery(id+"F4.wireOp",EDGE,"E10.sketch_text.stroke-46")])]});
            var Q116;
            Q116=makeQuery(id+"F5.opExtrude","CAP_FACE",FACE,{"disambiguationData":[OSD([sQuery(id+"F4.wireOp",EDGE,"E10.sketch_text.stroke-61"),sQuery(id+"F4.wireOp",EDGE,"E10.sketch_text.stroke-62"),sQuery(id+"F4.wireOp",EDGE,"E10.sketch_text.stroke-63"),sQuery(id+"F4.wireOp",EDGE,"E10.sketch_text.stroke-64"),sQuery(id+"F4.wireOp",EDGE,"E10.sketch_text.stroke-65"),sQuery(id+"F4.wireOp",EDGE,"E10.sketch_text.stroke-66"),sQuery(id+"F4.wireOp",EDGE,"E10.sketch_text.stroke-67"),sQuery(id+"F4.wireOp",EDGE,"E10.sketch_text.stroke-68"),sQuery(id+"F4.wireOp",EDGE,"E10.sketch_text.stroke-69"),sQuery(id+"F4.wireOp",EDGE,"E10.sketch_text.stroke-70"),sQuery(id+"F4.wireOp",EDGE,"E10.sketch_text.stroke-71"),sQuery(id+"F4.wireOp",EDGE,"E10.sketch_text.stroke-72"),sQuery(id+"F4.wireOp",EDGE,"E10.sketch_text.stroke-73"),sQuery(id+"F4.wireOp",EDGE,"E10.sketch_text.stroke-74"),sQuery(id+"F4.wireOp",EDGE,"E10.sketch_text.stroke-75"),sQuery(id+"F4.wireOp",EDGE,"E10.sketch_text.stroke-76"),sQuery(id+"F4.wireOp",EDGE,"E10.sketch_text.stroke-77"),sQuery(id+"F4.wireOp",EDGE,"E10.sketch_text.stroke-78"),sQuery(id+"F4.wireOp",EDGE,"E10.sketch_text.stroke-79"),sQuery(id+"F4.wireOp",EDGE,"E10.sketch_text.stroke-80"),sQuery(id+"F4.wireOp",EDGE,"E10.sketch_text.stroke-81"),sQuery(id+"F4.wireOp",EDGE,"E10.sketch_text.stroke-82"),sQuery(id+"F4.wireOp",EDGE,"E10.sketch_text.stroke-83"),sQuery(id+"F4.wireOp",EDGE,"E10.sketch_text.stroke-84"),sQuery(id+"F4.wireOp",EDGE,"E10.sketch_text.stroke-85"),sQuery(id+"F4.wireOp",EDGE,"E10.sketch_text.stroke-86"),sQuery(id+"F4.wireOp",EDGE,"E10.sketch_text.stroke-87"),sQuery(id+"F4.wireOp",EDGE,"E10.sketch_text.stroke-88"),sQuery(id+"F4.wireOp",EDGE,"E10.sketch_text.stroke-89"),sQuery(id+"F4.wireOp",EDGE,"E10.sketch_text.stroke-90"),sQuery(id+"F4.wireOp",EDGE,"E10.sketch_text.stroke-91"),sQuery(id+"F4.wireOp",EDGE,"E10.sketch_text.stroke-92"),sQuery(id+"F4.wireOp",EDGE,"E10.sketch_text.stroke-93"),sQuery(id+"F4.wireOp",EDGE,"E10.sketch_text.stroke-94"),sQuery(id+"F4.wireOp",EDGE,"E10.sketch_text.stroke-95"),sQuery(id+"F4.wireOp",EDGE,"E10.sketch_text.stroke-96"),sQuery(id+"F4.wireOp",EDGE,"E10.sketch_text.stroke-97"),sQuery(id+"F4.wireOp",EDGE,"E10.sketch_text.stroke-98"),sQuery(id+"F4.wireOp",EDGE,"E10.sketch_text.stroke-99"),sQuery(id+"F4.wireOp",EDGE,"E10.sketch_text.stroke-100"),sQuery(id+"F4.wireOp",EDGE,"E10.sketch_text.stroke-101"),sQuery(id+"F4.wireOp",EDGE,"E10.sketch_text.stroke-102"),sQuery(id+"F4.wireOp",EDGE,"E10.sketch_text.stroke-103"),sQuery(id+"F4.wireOp",EDGE,"E10.sketch_text.stroke-104")])],"isStart":false});
            var Q117;
            Q117=makeQuery(id+"F5.opExtrude","SWEPT_FACE",FACE,{"disambiguationData":[OSD([sQuery(id+"F4.wireOp",EDGE,"E10.sketch_text.stroke-33")])]});
            var Q118;
            Q118=makeQuery(id+"F5.opExtrude","SWEPT_FACE",FACE,{"disambiguationData":[OSD([sQuery(id+"F4.wireOp",EDGE,"E10.sketch_text.stroke-93")])]});
            var Q119;
            Q119=makeQuery(id+"F5.opExtrude","SWEPT_FACE",FACE,{"disambiguationData":[OSD([sQuery(id+"F4.wireOp",EDGE,"E10.sketch_text.stroke-34")])]});
            var Q120;
            Q120=makeQuery(id+"F5.opExtrude","SWEPT_FACE",FACE,{"disambiguationData":[OSD([sQuery(id+"F4.wireOp",EDGE,"E10.sketch_text.stroke-152")])]});
            var Q121;
            Q121=makeQuery(id+"F5.opExtrude","SWEPT_FACE",FACE,{"disambiguationData":[OSD([sQuery(id+"F4.wireOp",EDGE,"E10.sketch_text.stroke-51")])]});
            var Q122;
            Q122=makeQuery(id+"F5.opExtrude","SWEPT_FACE",FACE,{"disambiguationData":[OSD([sQuery(id+"F4.wireOp",EDGE,"E10.sketch_text.stroke-6")])]});
            var Q123;
            Q123=makeQuery(id+"F5.opExtrude","SWEPT_FACE",FACE,{"disambiguationData":[OSD([sQuery(id+"F4.wireOp",EDGE,"E10.sketch_text.stroke-7")])]});
            var Q124;
            Q124=makeQuery(id+"F5.opExtrude","SWEPT_FACE",FACE,{"disambiguationData":[OSD([sQuery(id+"F4.wireOp",EDGE,"E10.sketch_text.stroke-156")])]});
            var Q125;
            Q125=makeQuery(id+"F5.opExtrude","SWEPT_FACE",FACE,{"disambiguationData":[OSD([sQuery(id+"F4.wireOp",EDGE,"E10.sketch_text.stroke-112")])]});
            var Q126;
            Q126=makeQuery(id+"F5.boolean.opBoolean","SPLIT",FACE,{"disambiguationData":[TD([makeQuery(id+"F5.opExtrude","SWEPT_FACE",FACE,{"disambiguationData":[OSD([sQuery(id+"F4.wireOp",EDGE,"E10.sketch_text.stroke-182")])]})])],"derivedFrom":makeQuery(id+"F1.opExtrude","CAP_FACE",FACE,{"disambiguationData":[OSD([sQuery(id+"F0.wireOp",EDGE,"E0.bottom"),sQuery(id+"F0.wireOp",EDGE,"E0.top"),sQuery(id+"F0.wireOp",EDGE,"E0.left"),sQuery(id+"F0.wireOp",EDGE,"E0.right"),sQuery(id+"F0.wireOp",EDGE,"E1"),sQuery(id+"F0.wireOp",EDGE,"E7.MirrorC"),sQuery(id+"F0.wireOp",EDGE,"E8.MirrorC"),sQuery(id+"F0.wireOp",EDGE,"E9.MirrorC")])],"isStart":true})});
            var Q127;
            Q127=makeQuery(id+"F5.opExtrude","SWEPT_FACE",FACE,{"disambiguationData":[OSD([sQuery(id+"F4.wireOp",EDGE,"E10.sketch_text.stroke-96")])]});
            var Q128;
            Q128=makeQuery(id+"F5.opExtrude","SWEPT_FACE",FACE,{"disambiguationData":[OSD([sQuery(id+"F4.wireOp",EDGE,"E10.sketch_text.stroke-114")])]});
            var Q129;
            Q129=makeQuery(id+"F5.opExtrude","SWEPT_FACE",FACE,{"disambiguationData":[OSD([sQuery(id+"F4.wireOp",EDGE,"E10.sketch_text.stroke-39")])]});
            var Q130;
            Q130=makeQuery(id+"F5.opExtrude","SWEPT_FACE",FACE,{"disambiguationData":[OSD([sQuery(id+"F4.wireOp",EDGE,"E10.sketch_text.stroke-13")])]});
            var Q131;
            Q131=makeQuery(id+"F5.opExtrude","SWEPT_FACE",FACE,{"disambiguationData":[OSD([sQuery(id+"F4.wireOp",EDGE,"E10.sketch_text.stroke-115")])]});
            var Q132;
            Q132=makeQuery(id+"F5.opExtrude","SWEPT_FACE",FACE,{"disambiguationData":[OSD([sQuery(id+"F4.wireOp",EDGE,"E10.sketch_text.stroke-56")])]});
            var Q133;
            Q133=makeQuery(id+"F5.opExtrude","SWEPT_FACE",FACE,{"disambiguationData":[OSD([sQuery(id+"F4.wireOp",EDGE,"E10.sketch_text.stroke-144")])]});
            var Q134;
            Q134=makeQuery(id+"F5.opExtrude","SWEPT_FACE",FACE,{"disambiguationData":[OSD([sQuery(id+"F4.wireOp",EDGE,"E10.sketch_text.stroke-190")])]});
            var Q135;
            Q135=makeQuery(id+"F5.opExtrude","SWEPT_FACE",FACE,{"disambiguationData":[OSD([sQuery(id+"F4.wireOp",EDGE,"E10.sketch_text.stroke-116")])]});
            var Q136;
            Q136=makeQuery(id+"F5.opExtrude","SWEPT_FACE",FACE,{"disambiguationData":[OSD([sQuery(id+"F4.wireOp",EDGE,"E10.sketch_text.stroke-41")])]});
            var Q137;
            Q137=makeQuery(id+"F5.opExtrude","SWEPT_FACE",FACE,{"disambiguationData":[OSD([sQuery(id+"F4.wireOp",EDGE,"E10.sketch_text.stroke-161")])]});
            var Q138;
            Q138=makeQuery(id+"F5.opExtrude","SWEPT_FACE",FACE,{"disambiguationData":[OSD([sQuery(id+"F4.wireOp",EDGE,"E10.sketch_text.stroke-146")])]});
            var Q139;
            Q139=makeQuery(id+"F5.opExtrude","SWEPT_FACE",FACE,{"disambiguationData":[OSD([sQuery(id+"F4.wireOp",EDGE,"E10.sketch_text.stroke-58")])]});
            var Q140;
            Q140=makeQuery(id+"F5.opExtrude","SWEPT_FACE",FACE,{"disambiguationData":[OSD([sQuery(id+"F4.wireOp",EDGE,"E10.sketch_text.stroke-105")])]});
            var Q141;
            Q141=makeQuery(id+"F5.opExtrude","SWEPT_FACE",FACE,{"disambiguationData":[OSD([sQuery(id+"F4.wireOp",EDGE,"E10.sketch_text.stroke-177")])]});
            var Q142;
            Q142=makeQuery(id+"F5.opExtrude","SWEPT_FACE",FACE,{"disambiguationData":[OSD([sQuery(id+"F4.wireOp",EDGE,"E10.sketch_text.stroke-77")])]});
            var Q143;
            Q143=makeQuery(id+"F5.opExtrude","SWEPT_FACE",FACE,{"disambiguationData":[OSD([sQuery(id+"F4.wireOp",EDGE,"E10.sketch_text.stroke-138")])]});
            var Q144;
            Q144=makeQuery(id+"F5.opExtrude","SWEPT_FACE",FACE,{"disambiguationData":[OSD([sQuery(id+"F4.wireOp",EDGE,"E10.sketch_text.stroke-111")])]});
            var Q145;
            Q145=makeQuery(id+"F5.opExtrude","SWEPT_FACE",FACE,{"disambiguationData":[OSD([sQuery(id+"F4.wireOp",EDGE,"E10.sketch_text.stroke-53")])]});
            var Q146;
            Q146=makeQuery(id+"F5.opExtrude","SWEPT_FACE",FACE,{"disambiguationData":[OSD([sQuery(id+"F4.wireOp",EDGE,"E10.sketch_text.stroke-141")])]});
            var Q147;
            Q147=makeQuery(id+"F5.opExtrude","SWEPT_FACE",FACE,{"disambiguationData":[OSD([sQuery(id+"F4.wireOp",EDGE,"E10.sketch_text.stroke-157")])]});
            var Q148;
            Q148=makeQuery(id+"F5.opExtrude","SWEPT_FACE",FACE,{"disambiguationData":[OSD([sQuery(id+"F4.wireOp",EDGE,"E10.sketch_text.stroke-64")])]});
            var Q149;
            Q149=makeQuery(id+"F5.boolean.opBoolean","SPLIT",FACE,{"disambiguationData":[TD([makeQuery(id+"F5.opExtrude","SWEPT_FACE",FACE,{"disambiguationData":[OSD([sQuery(id+"F4.wireOp",EDGE,"E10.sketch_text.stroke-53")])]})])],"derivedFrom":makeQuery(id+"F1.opExtrude","CAP_FACE",FACE,{"disambiguationData":[OSD([sQuery(id+"F0.wireOp",EDGE,"E0.bottom"),sQuery(id+"F0.wireOp",EDGE,"E0.top"),sQuery(id+"F0.wireOp",EDGE,"E0.left"),sQuery(id+"F0.wireOp",EDGE,"E0.right"),sQuery(id+"F0.wireOp",EDGE,"E1"),sQuery(id+"F0.wireOp",EDGE,"E7.MirrorC"),sQuery(id+"F0.wireOp",EDGE,"E8.MirrorC"),sQuery(id+"F0.wireOp",EDGE,"E9.MirrorC")])],"isStart":true})});
            var Q150;
            Q150=makeQuery(id+"F5.opExtrude","SWEPT_FACE",FACE,{"disambiguationData":[OSD([sQuery(id+"F4.wireOp",EDGE,"E10.sketch_text.stroke-36")])]});
            var Q151;
            Q151=makeQuery(id+"F5.opExtrude","SWEPT_FACE",FACE,{"disambiguationData":[OSD([sQuery(id+"F4.wireOp",EDGE,"E10.sketch_text.stroke-22")])]});
            var Q152;
            Q152=makeQuery(id+"F5.boolean.opBoolean","SPLIT",FACE,{"disambiguationData":[TD([makeQuery(id+"F5.opExtrude","SWEPT_FACE",FACE,{"disambiguationData":[OSD([sQuery(id+"F4.wireOp",EDGE,"E10.sketch_text.stroke-119")])]})])],"derivedFrom":makeQuery(id+"F1.opExtrude","CAP_FACE",FACE,{"disambiguationData":[OSD([sQuery(id+"F0.wireOp",EDGE,"E0.bottom"),sQuery(id+"F0.wireOp",EDGE,"E0.top"),sQuery(id+"F0.wireOp",EDGE,"E0.left"),sQuery(id+"F0.wireOp",EDGE,"E0.right"),sQuery(id+"F0.wireOp",EDGE,"E1"),sQuery(id+"F0.wireOp",EDGE,"E7.MirrorC"),sQuery(id+"F0.wireOp",EDGE,"E8.MirrorC"),sQuery(id+"F0.wireOp",EDGE,"E9.MirrorC")])],"isStart":true})});
            var Q153;
            Q153=makeQuery(id+"F5.boolean.opBoolean","SPLIT",FACE,{"disambiguationData":[TD([makeQuery(id+"F5.opExtrude","SWEPT_FACE",FACE,{"disambiguationData":[OSD([sQuery(id+"F4.wireOp",EDGE,"E10.sketch_text.stroke-158")])]})])],"derivedFrom":makeQuery(id+"F1.opExtrude","CAP_FACE",FACE,{"disambiguationData":[OSD([sQuery(id+"F0.wireOp",EDGE,"E0.bottom"),sQuery(id+"F0.wireOp",EDGE,"E0.top"),sQuery(id+"F0.wireOp",EDGE,"E0.left"),sQuery(id+"F0.wireOp",EDGE,"E0.right"),sQuery(id+"F0.wireOp",EDGE,"E1"),sQuery(id+"F0.wireOp",EDGE,"E7.MirrorC"),sQuery(id+"F0.wireOp",EDGE,"E8.MirrorC"),sQuery(id+"F0.wireOp",EDGE,"E9.MirrorC")])],"isStart":true})});
            var Q154;
            Q154=makeQuery(id+"F5.opExtrude","SWEPT_FACE",FACE,{"disambiguationData":[OSD([sQuery(id+"F4.wireOp",EDGE,"E10.sketch_text.stroke-9")])]});
            var Q155;
            Q155=makeQuery(id+"F5.opExtrude","SWEPT_FACE",FACE,{"disambiguationData":[OSD([sQuery(id+"F4.wireOp",EDGE,"E10.sketch_text.stroke-167")])]});
            var Q156;
            Q156=makeQuery(id+"F5.opExtrude","SWEPT_FACE",FACE,{"disambiguationData":[OSD([sQuery(id+"F4.wireOp",EDGE,"E10.sketch_text.stroke-95")])]});
            var Q157;
            Q157=makeQuery(id+"F5.opExtrude","SWEPT_FACE",FACE,{"disambiguationData":[OSD([sQuery(id+"F4.wireOp",EDGE,"E10.sketch_text.stroke-184")])]});
            var Q158;
            Q158=makeQuery(id+"F5.opExtrude","SWEPT_FACE",FACE,{"disambiguationData":[OSD([sQuery(id+"F4.wireOp",EDGE,"E10.sketch_text.stroke-84")])]});
            var Q159;
            Q159=makeQuery(id+"F5.opExtrude","SWEPT_FACE",FACE,{"disambiguationData":[OSD([sQuery(id+"F4.wireOp",EDGE,"E10.sketch_text.stroke-68")])]});
            var Q160;
            Q160=makeQuery(id+"F5.opExtrude","SWEPT_FACE",FACE,{"disambiguationData":[OSD([sQuery(id+"F4.wireOp",EDGE,"E10.sketch_text.stroke-143")])]});
            var Q161;
            Q161=makeQuery(id+"F5.opExtrude","SWEPT_FACE",FACE,{"disambiguationData":[OSD([sQuery(id+"F4.wireOp",EDGE,"E10.sketch_text.stroke-189")])]});
            var Q162;
            Q162=makeQuery(id+"F5.opExtrude","CAP_FACE",FACE,{"disambiguationData":[OSD([sQuery(id+"F4.wireOp",EDGE,"E10.sketch_text.stroke-13"),sQuery(id+"F4.wireOp",EDGE,"E10.sketch_text.stroke-14"),sQuery(id+"F4.wireOp",EDGE,"E10.sketch_text.stroke-15"),sQuery(id+"F4.wireOp",EDGE,"E10.sketch_text.stroke-16"),sQuery(id+"F4.wireOp",EDGE,"E10.sketch_text.stroke-17"),sQuery(id+"F4.wireOp",EDGE,"E10.sketch_text.stroke-18"),sQuery(id+"F4.wireOp",EDGE,"E10.sketch_text.stroke-19"),sQuery(id+"F4.wireOp",EDGE,"E10.sketch_text.stroke-20")])],"isStart":false});
            var Q163;
            Q163=makeQuery(id+"F5.opExtrude","SWEPT_FACE",FACE,{"disambiguationData":[OSD([sQuery(id+"F4.wireOp",EDGE,"E10.sketch_text.stroke-57")])]});
            var Q164;
            Q164=makeQuery(id+"F5.opExtrude","SWEPT_FACE",FACE,{"disambiguationData":[OSD([sQuery(id+"F4.wireOp",EDGE,"E10.sketch_text.stroke-29")])]});
            var Q165;
            Q165=makeQuery(id+"F5.opExtrude","SWEPT_FACE",FACE,{"disambiguationData":[OSD([sQuery(id+"F4.wireOp",EDGE,"E10.sketch_text.stroke-60")])]});
            var Q166;
            Q166=makeQuery(id+"F5.opExtrude","SWEPT_FACE",FACE,{"disambiguationData":[OSD([sQuery(id+"F4.wireOp",EDGE,"E10.sketch_text.stroke-148")])]});
            var Q167;
            Q167=makeQuery(id+"F5.opExtrude","SWEPT_FACE",FACE,{"disambiguationData":[OSD([sQuery(id+"F4.wireOp",EDGE,"E10.sketch_text.stroke-75")])]});
            var Q168;
            Q168=makeQuery(id+"F5.opExtrude","SWEPT_FACE",FACE,{"disambiguationData":[OSD([sQuery(id+"F4.wireOp",EDGE,"E10.sketch_text.stroke-91")])]});
            var Q169;
            Q169=makeQuery(id+"F5.opExtrude","SWEPT_FACE",FACE,{"disambiguationData":[OSD([sQuery(id+"F4.wireOp",EDGE,"E10.sketch_text.stroke-78")])]});
            var Q170;
            Q170=makeQuery(id+"F5.opExtrude","SWEPT_FACE",FACE,{"disambiguationData":[OSD([sQuery(id+"F4.wireOp",EDGE,"E10.sketch_text.stroke-62")])]});
            var Q171;
            Q171=makeQuery(id+"F5.opExtrude","SWEPT_FACE",FACE,{"disambiguationData":[OSD([sQuery(id+"F4.wireOp",EDGE,"E10.sketch_text.stroke-182")])]});
            var Q172;
            Q172=makeQuery(id+"F5.opExtrude","SWEPT_FACE",FACE,{"disambiguationData":[OSD([sQuery(id+"F4.wireOp",EDGE,"E10.sketch_text.stroke-11")])]});
            var Q173;
            Q173=makeQuery(id+"F5.opExtrude","SWEPT_FACE",FACE,{"disambiguationData":[OSD([sQuery(id+"F4.wireOp",EDGE,"E10.sketch_text.stroke-97")])]});
            var Q174;
            Q174=makeQuery(id+"F5.opExtrude","SWEPT_FACE",FACE,{"disambiguationData":[OSD([sQuery(id+"F4.wireOp",EDGE,"E10.sketch_text.stroke-23")])]});
            var Q175;
            Q175=makeQuery(id+"F5.opExtrude","SWEPT_FACE",FACE,{"disambiguationData":[OSD([sQuery(id+"F4.wireOp",EDGE,"E10.sketch_text.stroke-80")])]});
            var Q176;
            Q176=makeQuery(id+"F5.boolean.opBoolean","SPLIT",FACE,{"disambiguationData":[TD([makeQuery(id+"F5.opExtrude","SWEPT_FACE",FACE,{"disambiguationData":[OSD([sQuery(id+"F4.wireOp",EDGE,"E10.sketch_text.stroke-99")])]})])],"derivedFrom":makeQuery(id+"F1.opExtrude","CAP_FACE",FACE,{"disambiguationData":[OSD([sQuery(id+"F0.wireOp",EDGE,"E0.bottom"),sQuery(id+"F0.wireOp",EDGE,"E0.top"),sQuery(id+"F0.wireOp",EDGE,"E0.left"),sQuery(id+"F0.wireOp",EDGE,"E0.right"),sQuery(id+"F0.wireOp",EDGE,"E1"),sQuery(id+"F0.wireOp",EDGE,"E7.MirrorC"),sQuery(id+"F0.wireOp",EDGE,"E8.MirrorC"),sQuery(id+"F0.wireOp",EDGE,"E9.MirrorC")])],"isStart":true})});
            var Q177;
            Q177=makeQuery(id+"F5.opExtrude","SWEPT_FACE",FACE,{"disambiguationData":[OSD([sQuery(id+"F4.wireOp",EDGE,"E10.sketch_text.stroke-168")])]});
            var Q178;
            Q178=makeQuery(id+"F5.opExtrude","SWEPT_FACE",FACE,{"disambiguationData":[OSD([sQuery(id+"F4.wireOp",EDGE,"E10.sketch_text.stroke-188")])]});
            var Q179;
            Q179=makeQuery(id+"F5.opExtrude","SWEPT_FACE",FACE,{"disambiguationData":[OSD([sQuery(id+"F4.wireOp",EDGE,"E10.sketch_text.stroke-129")])]});
            var Q180;
            Q180=makeQuery(id+"F5.opExtrude","SWEPT_FACE",FACE,{"disambiguationData":[OSD([sQuery(id+"F4.wireOp",EDGE,"E10.sketch_text.stroke-27")])]});
            var Q181;
            Q181=makeQuery(id+"F5.opExtrude","SWEPT_FACE",FACE,{"disambiguationData":[OSD([sQuery(id+"F4.wireOp",EDGE,"E10.sketch_text.stroke-175")])]});
            var Q182;
            Q182=makeQuery(id+"F5.opExtrude","SWEPT_FACE",FACE,{"disambiguationData":[OSD([sQuery(id+"F4.wireOp",EDGE,"E10.sketch_text.stroke-42")])]});
            var Q183;
            Q183=makeQuery(id+"F5.opExtrude","SWEPT_FACE",FACE,{"disambiguationData":[OSD([sQuery(id+"F4.wireOp",EDGE,"E10.sketch_text.stroke-118")])]});
            var Q184;
            Q184=makeQuery(id+"F5.opExtrude","SWEPT_FACE",FACE,{"disambiguationData":[OSD([sQuery(id+"F4.wireOp",EDGE,"E10.sketch_text.stroke-151")])]});
            var Q185;
            Q185=makeQuery(id+"F5.opExtrude","SWEPT_FACE",FACE,{"disambiguationData":[OSD([sQuery(id+"F4.wireOp",EDGE,"E10.sketch_text.stroke-137")])]});
            var Q186;
            Q186=makeQuery(id+"F5.opExtrude","SWEPT_FACE",FACE,{"disambiguationData":[OSD([sQuery(id+"F4.wireOp",EDGE,"E10.sketch_text.stroke-83")])]});
            var Q187;
            Q187=makeQuery(id+"F5.boolean.opBoolean","SPLIT",FACE,{"disambiguationData":[TD([makeQuery(id+"F5.opExtrude","SWEPT_FACE",FACE,{"disambiguationData":[OSD([sQuery(id+"F4.wireOp",EDGE,"E10.sketch_text.stroke-90")])]})])],"derivedFrom":makeQuery(id+"F1.opExtrude","CAP_FACE",FACE,{"disambiguationData":[OSD([sQuery(id+"F0.wireOp",EDGE,"E0.bottom"),sQuery(id+"F0.wireOp",EDGE,"E0.top"),sQuery(id+"F0.wireOp",EDGE,"E0.left"),sQuery(id+"F0.wireOp",EDGE,"E0.right"),sQuery(id+"F0.wireOp",EDGE,"E1"),sQuery(id+"F0.wireOp",EDGE,"E7.MirrorC"),sQuery(id+"F0.wireOp",EDGE,"E8.MirrorC"),sQuery(id+"F0.wireOp",EDGE,"E9.MirrorC")])],"isStart":true})});
            var Q188;
            Q188=makeQuery(id+"F5.opExtrude","SWEPT_FACE",FACE,{"disambiguationData":[OSD([sQuery(id+"F4.wireOp",EDGE,"E10.sketch_text.stroke-139")])]});
            var Q189;
            Q189=makeQuery(id+"F5.opExtrude","SWEPT_FACE",FACE,{"disambiguationData":[OSD([sQuery(id+"F4.wireOp",EDGE,"E10.sketch_text.stroke-70")])]});
            var Q190;
            Q190=makeQuery(id+"F5.opExtrude","SWEPT_FACE",FACE,{"disambiguationData":[OSD([sQuery(id+"F4.wireOp",EDGE,"E10.sketch_text.stroke-160")])]});
            var Q191;
            Q191=makeQuery(id+"F5.opExtrude","SWEPT_FACE",FACE,{"disambiguationData":[OSD([sQuery(id+"F4.wireOp",EDGE,"E10.sketch_text.stroke-71")])]});
            var Q192;
            Q192=makeQuery(id+"F5.opExtrude","SWEPT_FACE",FACE,{"disambiguationData":[OSD([sQuery(id+"F4.wireOp",EDGE,"E10.sketch_text.stroke-117")])]});
            var Q193;
            Q193=makeQuery(id+"F5.opExtrude","SWEPT_FACE",FACE,{"disambiguationData":[OSD([sQuery(id+"F4.wireOp",EDGE,"E10.sketch_text.stroke-147")])]});
            var Q194;
            Q194=makeQuery(id+"F5.opExtrude","SWEPT_FACE",FACE,{"disambiguationData":[OSD([sQuery(id+"F4.wireOp",EDGE,"E10.sketch_text.stroke-164")])]});
            var Q195;
            Q195=makeQuery(id+"F5.opExtrude","SWEPT_FACE",FACE,{"disambiguationData":[OSD([sQuery(id+"F4.wireOp",EDGE,"E10.sketch_text.stroke-61")])]});
            var Q196;
            Q196=makeQuery(id+"F5.opExtrude","SWEPT_FACE",FACE,{"disambiguationData":[OSD([sQuery(id+"F4.wireOp",EDGE,"E10.sketch_text.stroke-19")])]});
            var Q197;
            Q197=makeQuery(id+"F5.opExtrude","SWEPT_FACE",FACE,{"disambiguationData":[OSD([sQuery(id+"F4.wireOp",EDGE,"E10.sketch_text.stroke-35")])]});
            var Q198;
            Q198=makeQuery(id+"F5.opExtrude","SWEPT_FACE",FACE,{"disambiguationData":[OSD([sQuery(id+"F4.wireOp",EDGE,"E10.sketch_text.stroke-140")])]});
            var Q199;
            Q199=makeQuery(id+"F5.opExtrude","SWEPT_FACE",FACE,{"disambiguationData":[OSD([sQuery(id+"F4.wireOp",EDGE,"E10.sketch_text.stroke-20")])]});
            var Q200;
            Q200=makeQuery(id+"F5.opExtrude","SWEPT_FACE",FACE,{"disambiguationData":[OSD([sQuery(id+"F4.wireOp",EDGE,"E10.sketch_text.stroke-16")])]});
            var Q201;
            Q201=makeQuery(id+"F5.opExtrude","SWEPT_FACE",FACE,{"disambiguationData":[OSD([sQuery(id+"F4.wireOp",EDGE,"E10.sketch_text.stroke-18")])]});
            var Q202;
            Q202=makeQuery(id+"F5.opExtrude","SWEPT_FACE",FACE,{"disambiguationData":[OSD([sQuery(id+"F4.wireOp",EDGE,"E10.sketch_text.stroke-17")])]});
            var Q203;
            Q203=qCreatedBy(makeId("Right.planeOp"),FACE);
            mirror(context, id + "F6", {"operationType" : NewBodyOperationType.ADD, "entities" : qUnion([Q0]), "faces" : qUnion([Q1, Q2, Q3, Q4, Q5, Q6, Q7, Q8, Q9, Q10, Q11, Q12, Q13, Q14, Q15, Q16, Q17, Q18, Q19, Q20, Q21, Q22, Q23, Q24, Q25, Q26, Q27, Q28, Q29, Q30, Q31, Q32, Q33, Q34, Q35, Q36, Q37, Q38, Q39, Q40, Q41, Q42, Q43, Q44, Q45, Q46, Q47, Q48, Q49, Q50, Q51, Q52, Q53, Q54, Q55, Q56, Q57, Q58, Q59, Q60, Q61, Q62, Q63, Q64, Q65, Q66, Q67, Q68, Q69, Q70, Q71, Q72, Q73, Q74, Q75, Q76, Q77, Q78, Q79, Q80, Q81, Q82, Q83, Q84, Q85, Q86, Q87, Q88, Q89, Q90, Q91, Q92, Q93, Q94, Q95, Q96, Q97, Q98, Q99, Q100, Q101, Q102, Q103, Q104, Q105, Q106, Q107, Q108, Q109, Q110, Q111, Q112, Q113, Q114, Q115, Q116, Q117, Q118, Q119, Q120, Q121, Q122, Q123, Q124, Q125, Q126, Q127, Q128, Q129, Q130, Q131, Q132, Q133, Q134, Q135, Q136, Q137, Q138, Q139, Q140, Q141, Q142, Q143, Q144, Q145, Q146, Q147, Q148, Q149, Q150, Q151, Q152, Q153, Q154, Q155, Q156, Q157, Q158, Q159, Q160, Q161, Q162, Q163, Q164, Q165, Q166, Q167, Q168, Q169, Q170, Q171, Q172, Q173, Q174, Q175, Q176, Q177, Q178, Q179, Q180, Q181, Q182, Q183, Q184, Q185, Q186, Q187, Q188, Q189, Q190, Q191, Q192, Q193, Q194, Q195, Q196, Q197, Q198, Q199, Q200, Q201, Q202]), "mirrorPlane" : qUnion([Q203])});
        }
    });
